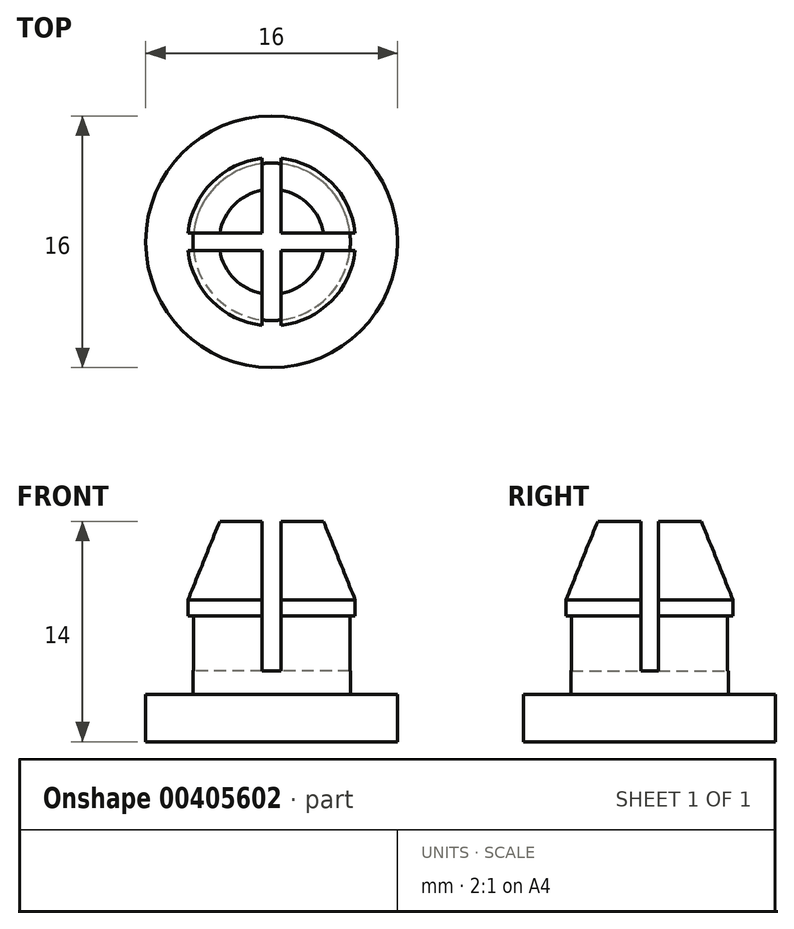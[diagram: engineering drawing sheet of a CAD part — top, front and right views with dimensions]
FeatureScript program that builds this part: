
annotation { "Feature Type Name" : "Feature", "Feature Type Description" : "" }
export const myFeature = defineFeature(function(context is Context, id is Id, definition is map)
    precondition{}
    {
        {
            var Q0;
            Q0=qCreatedBy(makeId("Top.planeOp"),FACE);
            var sketch = newSketch(context, id + "F0", { "sketchPlane" : qUnion([Q0])});
            skCircle(sketch, "E0", {"center": v(0, 0) * mm, "radius": 5 * mm});
            skCircle(sketch, "E1", {"center": v(0, 0) * mm, "radius": 6 * mm});
            skCircle(sketch, "E2", {"center": v(0, 0) * mm, "radius": 5.34 * mm});
            skCircle(sketch, "E3", {"center": v(0, 0) * mm, "radius": 8 * mm});
            skSolve(sketch);
        }
        {
            var Q0;
            Q0=makeQuery(id+"F0.imprint","IMPRINT",FACE,{"disambiguationData":[TD([[makeQuery(id+"F0.imprint","IMPRINT",EDGE,{"derivedFrom":sQuery(id+"F0.wireOp",EDGE,"E0")}),1.0]])]});
            extrude(context, id + "F1", {"entities" : qUnion([Q0]), "depth" : 12 * mm});
        }
        {
            var Q0;
            Q0=makeQuery(id+"F0.imprint","IMPRINT",FACE,{"disambiguationData":[TD([[makeQuery(id+"F0.imprint","IMPRINT",EDGE,{"derivedFrom":sQuery(id+"F0.wireOp",EDGE,"E0")}),-1.0]])]});
            extrude(context, id + "F2", {"entities" : qUnion([Q0]), "operationType" : NewBodyOperationType.ADD, "depth" : 12 * mm});
        }
        {
            var Q0;
            Q0=makeQuery(id+"F0.imprint","IMPRINT",FACE,{"disambiguationData":[TD([[makeQuery(id+"F0.imprint","IMPRINT",EDGE,{"derivedFrom":sQuery(id+"F0.wireOp",EDGE,"E0")}),-1.0]])]});
            extrude(context, id + "F3", {"entities" : qUnion([Q0]), "operationType" : NewBodyOperationType.REMOVE, "depth" : 6 * mm});
        }
        {
            var Q0;
            Q0=makeQuery(id+"F0.imprint","IMPRINT",FACE,{"disambiguationData":[TD([[makeQuery(id+"F0.imprint","IMPRINT",EDGE,{"derivedFrom":sQuery(id+"F0.wireOp",EDGE,"E0")}),-1.0]])]});
            var Q1;
            Q1=makeQuery(id+"F0.imprint","IMPRINT",FACE,{"disambiguationData":[TD([[makeQuery(id+"F0.imprint","IMPRINT",EDGE,{"derivedFrom":sQuery(id+"F0.wireOp",EDGE,"E1")}),-1.0]])]});
            extrude(context, id + "F4", {"entities" : qUnion([Q0, Q1]), "operationType" : NewBodyOperationType.ADD, "depth" : 1 * mm});
        }
        {
            var Q0;
            Q0=makeQuery(id+"F0.imprint","IMPRINT",FACE,{"disambiguationData":[TD([[makeQuery(id+"F0.imprint","IMPRINT",EDGE,{"derivedFrom":sQuery(id+"F0.wireOp",EDGE,"E2")}),-1.0]])]});
            extrude(context, id + "F5", {"entities" : qUnion([Q0]), "operationType" : NewBodyOperationType.ADD, "depth" : 1 * mm});
        }
        {
            var Q0;
            Q0=qCreatedBy(makeId("Top.planeOp"),FACE);
            cPlane(context, id + "F6", {"entities" : qUnion([Q0]), "cplaneType" : CPlaneType.OFFSET, "offset" : 12.5 * mm, "width" : 150 * mm, "height" : 150 * mm});
        }
        {
            var Q0;
            Q0=qCreatedBy(id+"F6.planeOp",FACE);
            var sketch = newSketch(context, id + "F7", { "sketchPlane" : qUnion([Q0])});
            skLineSegment(sketch, "E4.bottom", {"start": v(0.6, -6.09) * mm, "end": v(-0.6, -6.09) * mm});
            skLineSegment(sketch, "E4.top", {"start": v(0.6, 6.09) * mm, "end": v(-0.6, 6.09) * mm});
            skLineSegment(sketch, "E4.left", {"start": v(0.6, -6.09) * mm, "end": v(0.6, -0.56) * mm});
            skLineSegment(sketch, "E4.right", {"start": v(-0.6, -6.09) * mm, "end": v(-0.6, -0.56) * mm});
            skPoint(sketch, "E4.middle", {"position": v(0, 0) * mm});
            skLineSegment(sketch, "E5.bottom", {"start": v(5.56, -0.56) * mm, "end": v(0.6, -0.56) * mm});
            skLineSegment(sketch, "E5.top", {"start": v(5.56, 0.56) * mm, "end": v(0.6, 0.56) * mm});
            skLineSegment(sketch, "E5.left", {"start": v(5.56, -0.56) * mm, "end": v(5.56, 0.56) * mm});
            skLineSegment(sketch, "E5.right", {"start": v(-5.56, -0.56) * mm, "end": v(-5.56, 0.56) * mm});
            skLineSegment(sketch, "E6.trimOffspring", {"start": v(0.6, 0.56) * mm, "end": v(0.6, 6.09) * mm});
            skLineSegment(sketch, "E7.trimOffspring", {"start": v(-0.6, -0.56) * mm, "end": v(-5.56, -0.56) * mm});
            skLineSegment(sketch, "E8.trimOffspring", {"start": v(-0.6, 0.56) * mm, "end": v(-0.6, 6.09) * mm});
            skLineSegment(sketch, "E9.trimOffspring", {"start": v(-0.6, 0.56) * mm, "end": v(-5.56, 0.56) * mm});
            skSolve(sketch);
        }
        {
            var Q0;
            Q0=makeQuery(id+"F7.imprint","IMPRINT",FACE,{"disambiguationData":[TD([[makeQuery(id+"F7.imprint","IMPRINT",EDGE,{"derivedFrom":sQuery(id+"F7.wireOp",EDGE,"E4.bottom")}),-1.0]])]});
            extrude(context, id + "F8", {"entities" : qUnion([Q0]), "operationType" : NewBodyOperationType.REMOVE, "oppositeDirection" : true, "depth" : 10 * mm});
        }
        {
            var Q0;
            {var subQ0=sQuery(id+"F0.wireOp",EDGE,"E2");Q0=makeQuery(id+"F8.boolean.opBoolean","SPLIT",EDGE,{"disambiguationData":[TD([makeQuery(id+"F8.opExtrude","SWEPT_FACE",FACE,{"disambiguationData":[OSD([sQuery(id+"F7.wireOp",EDGE,"E4.left")])]})])],"derivedFrom":makeQuery(id+"F2.opExtrude","CAP_EDGE",EDGE,{"disambiguationData":[OSD([subQ0])],"isStart":false})});}
            var Q1;
            {var subQ0=sQuery(id+"F0.wireOp",EDGE,"E2");Q1=makeQuery(id+"F8.boolean.opBoolean","SPLIT",EDGE,{"disambiguationData":[TD([makeQuery(id+"F8.opExtrude","SWEPT_FACE",FACE,{"disambiguationData":[OSD([sQuery(id+"F7.wireOp",EDGE,"E4.right")])]})])],"derivedFrom":makeQuery(id+"F2.opExtrude","CAP_EDGE",EDGE,{"disambiguationData":[OSD([subQ0])],"isStart":false})});}
            var Q2;
            {var subQ0=sQuery(id+"F0.wireOp",EDGE,"E2");Q2=makeQuery(id+"F8.boolean.opBoolean","SPLIT",EDGE,{"disambiguationData":[TD([makeQuery(id+"F8.opExtrude","SWEPT_FACE",FACE,{"disambiguationData":[OSD([sQuery(id+"F7.wireOp",EDGE,"E5.top")])]})])],"derivedFrom":makeQuery(id+"F2.opExtrude","CAP_EDGE",EDGE,{"disambiguationData":[OSD([subQ0])],"isStart":false})});}
            var Q3;
            {var subQ0=sQuery(id+"F0.wireOp",EDGE,"E2");Q3=makeQuery(id+"F8.boolean.opBoolean","SPLIT",EDGE,{"disambiguationData":[TD([makeQuery(id+"F8.opExtrude","SWEPT_FACE",FACE,{"disambiguationData":[OSD([sQuery(id+"F7.wireOp",EDGE,"E8.trimOffspring")])]})])],"derivedFrom":makeQuery(id+"F2.opExtrude","CAP_EDGE",EDGE,{"disambiguationData":[OSD([subQ0])],"isStart":false})});}
            chamfer(context, id + "F9", {"entities" : qUnion([Q0, Q1, Q2, Q3]), "chamferType" : ChamferType.TWO_OFFSETS, "width1" : 2 * mm, "oppositeDirection" : false, "width2" : 5 * mm, "tangentPropagation" : true});
        }
        {
            var Q0;
            Q0=makeQuery(id+"F0.imprint","IMPRINT",FACE,{"disambiguationData":[TD([[makeQuery(id+"F0.imprint","IMPRINT",EDGE,{"derivedFrom":sQuery(id+"F0.wireOp",EDGE,"E0")}),1.0]])]});
            var Q1;
            Q1=makeQuery(id+"F0.imprint","IMPRINT",FACE,{"disambiguationData":[TD([[makeQuery(id+"F0.imprint","IMPRINT",EDGE,{"derivedFrom":sQuery(id+"F0.wireOp",EDGE,"E0")}),-1.0]])]});
            var Q2;
            Q2=makeQuery(id+"F0.imprint","IMPRINT",FACE,{"disambiguationData":[TD([[makeQuery(id+"F0.imprint","IMPRINT",EDGE,{"derivedFrom":sQuery(id+"F0.wireOp",EDGE,"E1")}),1.0]])]});
            var Q3;
            Q3=makeQuery(id+"F0.imprint","IMPRINT",FACE,{"disambiguationData":[TD([[makeQuery(id+"F0.imprint","IMPRINT",EDGE,{"derivedFrom":sQuery(id+"F0.wireOp",EDGE,"E1")}),-1.0]])]});
            extrude(context, id + "F10", {"entities" : qUnion([Q0, Q1, Q2, Q3]), "operationType" : NewBodyOperationType.ADD, "oppositeDirection" : true, "depth" : 2 * mm});
        }
    });
